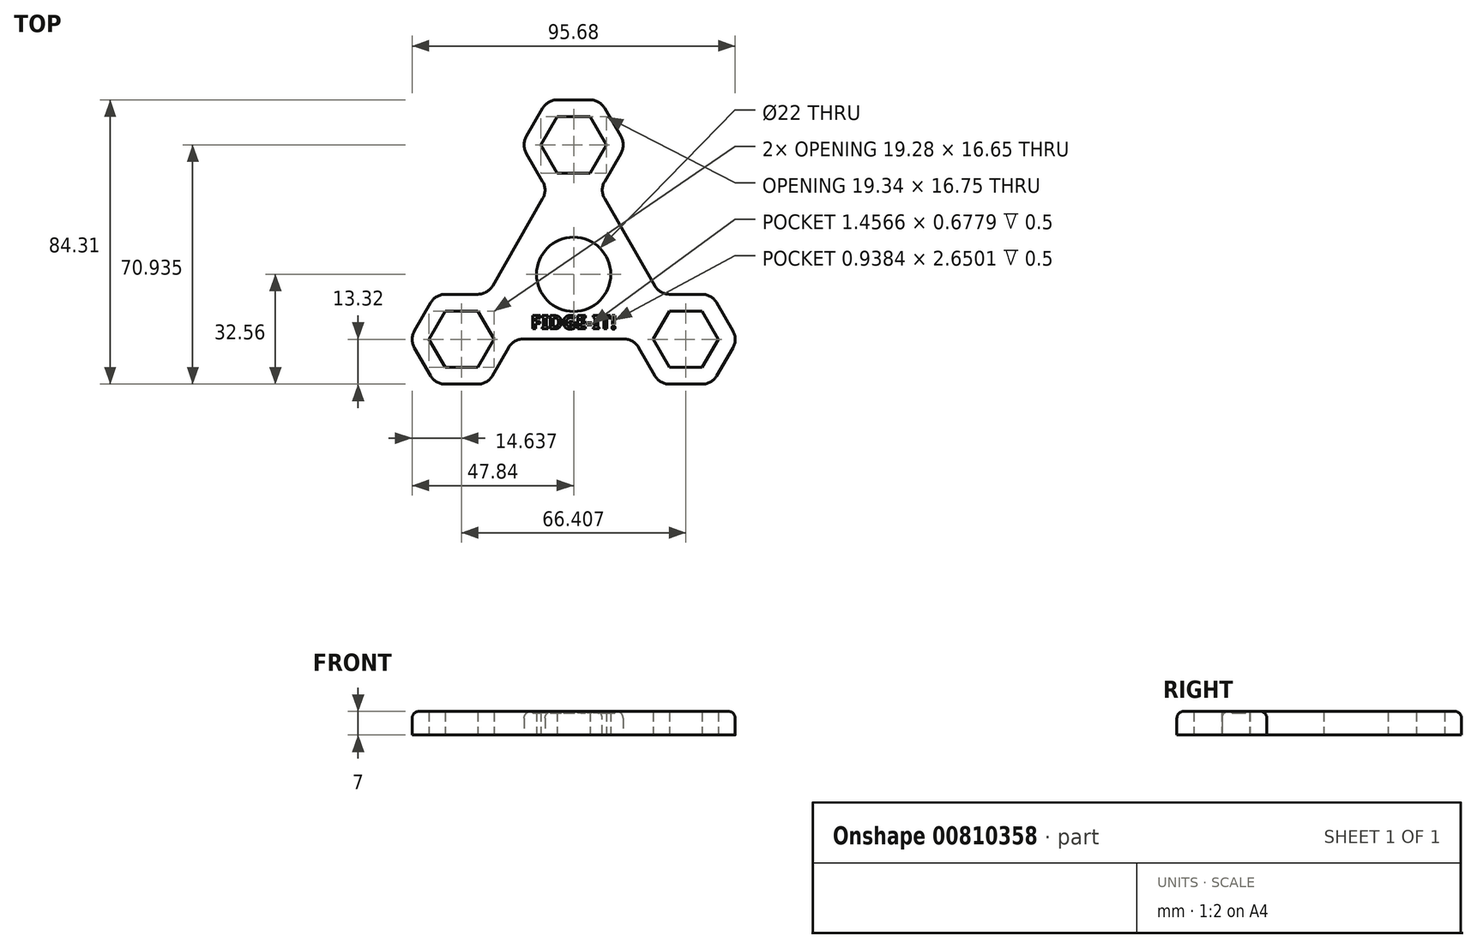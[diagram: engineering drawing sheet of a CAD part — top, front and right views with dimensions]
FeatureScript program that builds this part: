
annotation { "Feature Type Name" : "Feature", "Feature Type Description" : "" }
export const myFeature = defineFeature(function(context is Context, id is Id, definition is map)
    precondition{}
    {
        {
            var Q0;
            Q0=qCreatedBy(makeId("Top.planeOp"),FACE);
            var sketch = newSketch(context, id + "F0", { "sketchPlane" : qUnion([Q0])});
            skCircle(sketch, "E0", {"center": v(0, 0) * mm, "radius": 11 * mm});
            skLineSegment(sketch, "E1.0", {"start": v(4.84, 30) * mm, "end": v(-4.84, 30) * mm});
            skLineSegment(sketch, "E1.1", {"start": v(-4.84, 30) * mm, "end": v(-9.67, 38.38) * mm});
            skLineSegment(sketch, "E1.2", {"start": v(-9.67, 38.38) * mm, "end": v(-4.84, 46.75) * mm});
            skLineSegment(sketch, "E1.3", {"start": v(-4.84, 46.75) * mm, "end": v(4.84, 46.75) * mm});
            skLineSegment(sketch, "E1.4", {"start": v(4.84, 46.75) * mm, "end": v(9.67, 38.37) * mm});
            skLineSegment(sketch, "E1.5", {"start": v(9.67, 38.37) * mm, "end": v(4.84, 30) * mm});
            skPoint(sketch, "E1.0.midPoint", {"position": v(0, 30) * mm});
            skLineSegment(sketch, "E2.2.0", {"start": v(42.84, -19.3) * mm, "end": v(38.07, -27.56) * mm});
            skLineSegment(sketch, "E2.2.1", {"start": v(28.4, -27.56) * mm, "end": v(23.56, -19.19) * mm});
            skLineSegment(sketch, "E2.2.2", {"start": v(38.07, -27.56) * mm, "end": v(28.4, -27.56) * mm});
            skLineSegment(sketch, "E2.2.3", {"start": v(38, -10.92) * mm, "end": v(42.84, -19.3) * mm});
            skPoint(sketch, "E2.2.5", {"position": v(25.98, -15) * mm});
            skLineSegment(sketch, "E2.2.6", {"start": v(28.34, -10.92) * mm, "end": v(38, -10.92) * mm});
            skLineSegment(sketch, "E2.2.7", {"start": v(23.56, -19.19) * mm, "end": v(28.34, -10.92) * mm});
            skPoint(sketch, "E1.cCircle.center.orphan", {"position": v(0, 38.38) * mm});
            skLineSegment(sketch, "E3.0", {"start": v(-7.72, 25) * mm, "end": v(-15.44, 38.38) * mm});
            skLineSegment(sketch, "E3.1", {"start": v(-7.72, 51.75) * mm, "end": v(7.72, 51.75) * mm});
            skLineSegment(sketch, "E3.2", {"start": v(7.72, 51.75) * mm, "end": v(15.44, 38.37) * mm});
            skLineSegment(sketch, "E3.3", {"start": v(-15.44, 38.38) * mm, "end": v(-7.72, 51.75) * mm});
            skLineSegment(sketch, "E3.4", {"start": v(15.44, 38.37) * mm, "end": v(7.72, 25) * mm});
            skLineSegment(sketch, "E4.0", {"start": v(25.51, -32.56) * mm, "end": v(17.79, -19.19) * mm});
            skLineSegment(sketch, "E4.1", {"start": v(25.45, -5.92) * mm, "end": v(40.9, -5.92) * mm});
            skLineSegment(sketch, "E4.2", {"start": v(40.9, -5.92) * mm, "end": v(48.62, -19.3) * mm});
            skLineSegment(sketch, "E4.4", {"start": v(48.62, -19.3) * mm, "end": v(40.96, -32.56) * mm});
            skLineSegment(sketch, "E4.5", {"start": v(40.96, -32.56) * mm, "end": v(25.51, -32.56) * mm});
            skLineSegment(sketch, "E5.MirrorCS", {"start": v(-23.56, -19.19) * mm, "end": v(-28.34, -10.92) * mm});
            skPoint(sketch, "E6.MirrorP", {"position": v(-25.98, -15) * mm});
            skLineSegment(sketch, "E7.MirrorCS", {"start": v(-28.34, -10.92) * mm, "end": v(-38, -10.92) * mm});
            skLineSegment(sketch, "E8.MirrorCS", {"start": v(-40.96, -32.56) * mm, "end": v(-25.51, -32.56) * mm});
            skLineSegment(sketch, "E9.MirrorCS", {"start": v(-42.84, -19.3) * mm, "end": v(-38.07, -27.56) * mm});
            skLineSegment(sketch, "E10.MirrorCS", {"start": v(-38, -10.92) * mm, "end": v(-42.84, -19.3) * mm});
            skLineSegment(sketch, "E11.MirrorCS", {"start": v(-25.51, -32.56) * mm, "end": v(-17.79, -19.19) * mm});
            skLineSegment(sketch, "E12.MirrorCS", {"start": v(-48.62, -19.3) * mm, "end": v(-40.96, -32.56) * mm});
            skLineSegment(sketch, "E13.MirrorCS", {"start": v(-40.9, -5.92) * mm, "end": v(-48.62, -19.3) * mm});
            skLineSegment(sketch, "E14.MirrorCS", {"start": v(-28.4, -27.56) * mm, "end": v(-23.56, -19.19) * mm});
            skLineSegment(sketch, "E15.MirrorCS", {"start": v(-38.07, -27.56) * mm, "end": v(-28.4, -27.56) * mm});
            skLineSegment(sketch, "E16.MirrorCS", {"start": v(-25.45, -5.92) * mm, "end": v(-40.9, -5.92) * mm});
            skLineSegment(sketch, "E17", {"start": v(-7.72, 25) * mm, "end": v(-25.45, -5.92) * mm});
            skLineSegment(sketch, "E18", {"start": v(7.72, 25) * mm, "end": v(25.45, -5.92) * mm});
            skLineSegment(sketch, "E19", {"start": v(17.79, -19.19) * mm, "end": v(-17.79, -19.19) * mm});
            skSolve(sketch);
        }
        {
            var Q0;
            Q0=makeQuery(id+"F0.imprint","IMPRINT",FACE,{"disambiguationData":[TD([[makeQuery(id+"F0.imprint","IMPRINT",EDGE,{"derivedFrom":sQuery(id+"F0.wireOp",EDGE,"E1.0")}),1.0]])]});
            extrude(context, id + "F1", {"entities" : qUnion([Q0]), "depth" : 7 * mm, "offsetDistance" : 25 * mm});
        }
        {
            var Q0;
            Q0=makeQuery(id+"F1.opExtrude","SWEPT_EDGE",EDGE,{"disambiguationData":[OSD([sQuery(id+"F0.wireOp",EDGE,"E8.MirrorCS"),sQuery(id+"F0.wireOp",EDGE,"E11.MirrorCS")])]});
            var Q1;
            Q1=makeQuery(id+"F1.opExtrude","SWEPT_EDGE",EDGE,{"disambiguationData":[OSD([sQuery(id+"F0.wireOp",EDGE,"E8.MirrorCS"),sQuery(id+"F0.wireOp",EDGE,"E12.MirrorCS")])]});
            var Q2;
            Q2=makeQuery(id+"F1.opExtrude","SWEPT_EDGE",EDGE,{"disambiguationData":[OSD([sQuery(id+"F0.wireOp",EDGE,"E12.MirrorCS"),sQuery(id+"F0.wireOp",EDGE,"E13.MirrorCS")])]});
            var Q3;
            Q3=makeQuery(id+"F1.opExtrude","SWEPT_EDGE",EDGE,{"disambiguationData":[OSD([sQuery(id+"F0.wireOp",EDGE,"E13.MirrorCS"),sQuery(id+"F0.wireOp",EDGE,"E16.MirrorCS")])]});
            var Q4;
            Q4=makeQuery(id+"F1.opExtrude","SWEPT_EDGE",EDGE,{"disambiguationData":[OSD([sQuery(id+"F0.wireOp",EDGE,"E16.MirrorCS"),sQuery(id+"F0.wireOp",EDGE,"E17")])]});
            var Q5;
            Q5=makeQuery(id+"F1.opExtrude","SWEPT_EDGE",EDGE,{"disambiguationData":[OSD([sQuery(id+"F0.wireOp",EDGE,"E11.MirrorCS"),sQuery(id+"F0.wireOp",EDGE,"E19")])]});
            var Q6;
            Q6=makeQuery(id+"F1.opExtrude","SWEPT_EDGE",EDGE,{"disambiguationData":[OSD([sQuery(id+"F0.wireOp",EDGE,"E4.0"),sQuery(id+"F0.wireOp",EDGE,"E19")])]});
            var Q7;
            Q7=makeQuery(id+"F1.opExtrude","SWEPT_EDGE",EDGE,{"disambiguationData":[OSD([sQuery(id+"F0.wireOp",EDGE,"E4.0"),sQuery(id+"F0.wireOp",EDGE,"E4.5")])]});
            var Q8;
            Q8=makeQuery(id+"F1.opExtrude","SWEPT_EDGE",EDGE,{"disambiguationData":[OSD([sQuery(id+"F0.wireOp",EDGE,"E4.4"),sQuery(id+"F0.wireOp",EDGE,"E4.5")])]});
            var Q9;
            Q9=makeQuery(id+"F1.opExtrude","SWEPT_EDGE",EDGE,{"disambiguationData":[OSD([sQuery(id+"F0.wireOp",EDGE,"E4.2"),sQuery(id+"F0.wireOp",EDGE,"E4.4")])]});
            var Q10;
            Q10=makeQuery(id+"F1.opExtrude","SWEPT_EDGE",EDGE,{"disambiguationData":[OSD([sQuery(id+"F0.wireOp",EDGE,"E4.1"),sQuery(id+"F0.wireOp",EDGE,"E4.2")])]});
            var Q11;
            Q11=makeQuery(id+"F1.opExtrude","SWEPT_EDGE",EDGE,{"disambiguationData":[OSD([sQuery(id+"F0.wireOp",EDGE,"E4.1"),sQuery(id+"F0.wireOp",EDGE,"E18")])]});
            var Q12;
            Q12=makeQuery(id+"F1.opExtrude","SWEPT_EDGE",EDGE,{"disambiguationData":[OSD([sQuery(id+"F0.wireOp",EDGE,"E3.4"),sQuery(id+"F0.wireOp",EDGE,"E18")])]});
            var Q13;
            Q13=makeQuery(id+"F1.opExtrude","SWEPT_EDGE",EDGE,{"disambiguationData":[OSD([sQuery(id+"F0.wireOp",EDGE,"E3.2"),sQuery(id+"F0.wireOp",EDGE,"E3.4")])]});
            var Q14;
            Q14=makeQuery(id+"F1.opExtrude","SWEPT_EDGE",EDGE,{"disambiguationData":[OSD([sQuery(id+"F0.wireOp",EDGE,"E3.1"),sQuery(id+"F0.wireOp",EDGE,"E3.2")])]});
            var Q15;
            Q15=makeQuery(id+"F1.opExtrude","SWEPT_EDGE",EDGE,{"disambiguationData":[OSD([sQuery(id+"F0.wireOp",EDGE,"E3.1"),sQuery(id+"F0.wireOp",EDGE,"E3.3")])]});
            var Q16;
            Q16=makeQuery(id+"F1.opExtrude","SWEPT_EDGE",EDGE,{"disambiguationData":[OSD([sQuery(id+"F0.wireOp",EDGE,"E3.0"),sQuery(id+"F0.wireOp",EDGE,"E3.3")])]});
            var Q17;
            Q17=makeQuery(id+"F1.opExtrude","SWEPT_EDGE",EDGE,{"disambiguationData":[OSD([sQuery(id+"F0.wireOp",EDGE,"E3.0"),sQuery(id+"F0.wireOp",EDGE,"E17")])]});
            fillet(context, id + "F2", {"entities" : qUnion([Q0, Q1, Q2, Q3, Q4, Q5, Q6, Q7, Q8, Q9, Q10, Q11, Q12, Q13, Q14, Q15, Q16, Q17]), "radius" : 5 * mm, "tangentPropagation" : true, "allowEdgeOverflow" : false});
        }
        {
            var Q0;
            Q0=makeQuery(id+"F1.opExtrude","CAP_EDGE",EDGE,{"disambiguationData":[OSD([sQuery(id+"F0.wireOp",EDGE,"E19")])],"isStart":false});
            fillet(context, id + "F3", {"entities" : qUnion([Q0]), "radius" : 2 * mm, "tangentPropagation" : true, "allowEdgeOverflow" : false});
        }
        {
            var Q0;
            Q0=makeQuery(id+"F1.opExtrude","CAP_FACE",FACE,{"disambiguationData":[OSD([sQuery(id+"F0.wireOp",EDGE,"E1.0"),sQuery(id+"F0.wireOp",EDGE,"E1.1"),sQuery(id+"F0.wireOp",EDGE,"E1.2"),sQuery(id+"F0.wireOp",EDGE,"E1.3"),sQuery(id+"F0.wireOp",EDGE,"E1.4"),sQuery(id+"F0.wireOp",EDGE,"E1.5"),sQuery(id+"F0.wireOp",EDGE,"E2.2.0"),sQuery(id+"F0.wireOp",EDGE,"E2.2.1"),sQuery(id+"F0.wireOp",EDGE,"E2.2.2"),sQuery(id+"F0.wireOp",EDGE,"E2.2.3"),sQuery(id+"F0.wireOp",EDGE,"E2.2.6"),sQuery(id+"F0.wireOp",EDGE,"E2.2.7"),sQuery(id+"F0.wireOp",EDGE,"E0"),sQuery(id+"F0.wireOp",EDGE,"E3.0"),sQuery(id+"F0.wireOp",EDGE,"E3.1"),sQuery(id+"F0.wireOp",EDGE,"E3.2"),sQuery(id+"F0.wireOp",EDGE,"E3.3"),sQuery(id+"F0.wireOp",EDGE,"E3.4"),sQuery(id+"F0.wireOp",EDGE,"E4.0"),sQuery(id+"F0.wireOp",EDGE,"E4.1"),sQuery(id+"F0.wireOp",EDGE,"E4.2"),sQuery(id+"F0.wireOp",EDGE,"E4.4"),sQuery(id+"F0.wireOp",EDGE,"E4.5"),sQuery(id+"F0.wireOp",EDGE,"E5.MirrorCS"),sQuery(id+"F0.wireOp",EDGE,"E7.MirrorCS"),sQuery(id+"F0.wireOp",EDGE,"E8.MirrorCS"),sQuery(id+"F0.wireOp",EDGE,"E9.MirrorCS"),sQuery(id+"F0.wireOp",EDGE,"E10.MirrorCS"),sQuery(id+"F0.wireOp",EDGE,"E11.MirrorCS"),sQuery(id+"F0.wireOp",EDGE,"E12.MirrorCS"),sQuery(id+"F0.wireOp",EDGE,"E13.MirrorCS"),sQuery(id+"F0.wireOp",EDGE,"E14.MirrorCS"),sQuery(id+"F0.wireOp",EDGE,"E15.MirrorCS"),sQuery(id+"F0.wireOp",EDGE,"E16.MirrorCS"),sQuery(id+"F0.wireOp",EDGE,"E17"),sQuery(id+"F0.wireOp",EDGE,"E18"),sQuery(id+"F0.wireOp",EDGE,"E19")])],"isStart":false});
            var sketch = newSketch(context, id + "F4", { "sketchPlane" : qUnion([Q0])});
            skText(sketch, "E20", { "text": "FIDGE-IT!", "fontName": "NotoSans-Bold.ttf"});
            const initialGuessF4  = {"E20": [-0.01263, -0.01619, 1, 0, 0.004]};
            skSetInitialGuess(sketch, initialGuessF4);
            skSolve(sketch);
        }
        {
            var Q0;
            Q0=qSketchRegion(id+"F4",true);
            extrude(context, id + "F5", {"entities" : qUnion([Q0]), "operationType" : NewBodyOperationType.REMOVE, "oppositeDirection" : true, "depth" : 0.5 * mm, "offsetDistance" : 25 * mm});
        }
    });
